# Revit family: Carrier_Closet_Offset_Vertical-Zurn-Z1209N
name_source: partatom
category: Plumbing Fixtures
units: mm (PartAtom-declared; Revit-internal decimal feet)

## family parameters
Always vertical = Yes
Cut with Voids When Loaded = No
Maintain Annotation Orientation = No
OmniClass Number = 23.45.55.11
OmniClass Title = Sanitary Components
Part Type = Normal
Room Calculation Point = No
Round Connector Dimension = Use Radius
Shared = No
Work Plane-Based = No

## types (2) — shared parameters
Approx. Weight (Lbs) = 67 "
CW Connection = No
Coupling Material = ABS - Zurn - Plastic
Coupling Radius = 2 "
Default Elevation = 2.375 "
Description = VERTICAL OFFSET SIPHON JET WATER CLOSET SUPPORT SYSTEM NO-HUB SERIES
Diemsion - E = 3.75 "
Diemsion - N = 6.75 "
Dimension - B = 24 "
HW Connection = No
Height = 16.75 "
Main Material = Iron - Zurn - Cast - Painted - Blue
Manufacturer = Zurn Water, LLC
Manufacurer Brand = Zurn
Model = Z1209-N
Modified Date = 11/07/2025
Outlet Pipe Radius (Inside) = 2.013 "
Outlet Pipe Radius (Nominal) = 2 "
Outlet Pipe Radius (Outer) = 2.25 "
Product Documentation Link = https://files.zurn.com
Product Installation Sheet URL = https://files.zurn.com
Product Page URL = https://www.zurn.com
Product data url = https://www.bimobject.com
URL = www.zurn.com
Vent Connection = No
Vent Pipe Radius (Inside) = 1.034 "
Vent Pipe Radius (Nominal) = 1 "
Vent Pipe Radius (Outer) = 1.188 "
WFU = 1
Waste Connection = Yes
Width = 18.875 "
zero-valued in all types: CWFU, HWFU

## per-type parameters (varying)
| type | Assembly Code | Horizontal Pipe_NL4 | Horizontal Pipe_NR4 | Masking region_NL4 | Masking region_NR4 | Model Lines_NL4 | Model lines_NR4 | Vent_NL4 | Vent_NR4 | Vertical Offset Pipe_NL4 | Vertical Offset Pipe_NR4 |
| Z1209-NL4 | D2010110 | Yes | No | Yes | No | Yes | No | Yes | No | Yes | No |
| Z1209-NR4 |  | No | Yes | No | Yes | No | Yes | No | Yes | No | Yes |

## geometry (parser evidence)
native form markers: Sweep x3
no freeform markers — native parametric forms only
